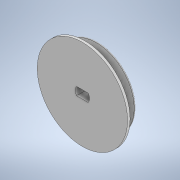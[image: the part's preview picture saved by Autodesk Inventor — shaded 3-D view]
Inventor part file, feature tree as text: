
AUTODESK INVENTOR PART (.ipt)
format: ipt  version: 2021 (Build 250183000, 183)  size: 174,080 bytes
history: native  units: mm
features: sketch x5, extrude x4, revolve x1, fillet x1
ambient origin geometry x8: Origin, YZ Plane, XZ Plane, XY Plane, X Axis, Y Axis, Z Axis, Center Point
bodies: Solid1 (feature_tree)
feature tree (11):
  extrude  "Extrusion1"  Depth=6.0mm TaperAngle=0.0deg
  extrude  "Extrusion2"  Depth=6.6mm TaperAngle=0.0deg
  extrude  "Extrusion3"  Depth=3.0mm
  revolve  "Revolution1"  [1 undecoded]
  fillet  "Fillet1"  Radius=3.0mm
  extrude  "Extrusion5"  Depth=0.3mm
  sketch  "Sketch1"  dims[d0=38.0mm d1=6.0mm d2=0.0mm]
  sketch  "Sketch2"  dims[d3=5.6mm d4=6.6mm d5=0.0mm]
  sketch  "Sketch3"  dims[d6=3.0mm d7=3.0mm]
  sketch  "Sketch5"  dims[d8=3.0mm d9=3.0mm d10=3.0mm]
  sketch  "Sketch6"  dims[d11=3.0mm d12=1.6mm d13=1.6mm d14=6.0mm d15=0.0mm d19=2.5mm d20=2.5mm d21=90.0deg d22=0.3mm d23=1.2mm d24=38.0mm d25=2.0mm d26=0.0mm d16=0.5mm d17=0.872665mm d18=0.5mm d27=0.5mm d28=0.872665mm d29=0.5mm d30=0.872665mm]
note: 1 required parameter value undecoded (feature->parameter linkage not recoverable at this tier; creation-order binding heuristic only, values carry confidence <= 0.55)
